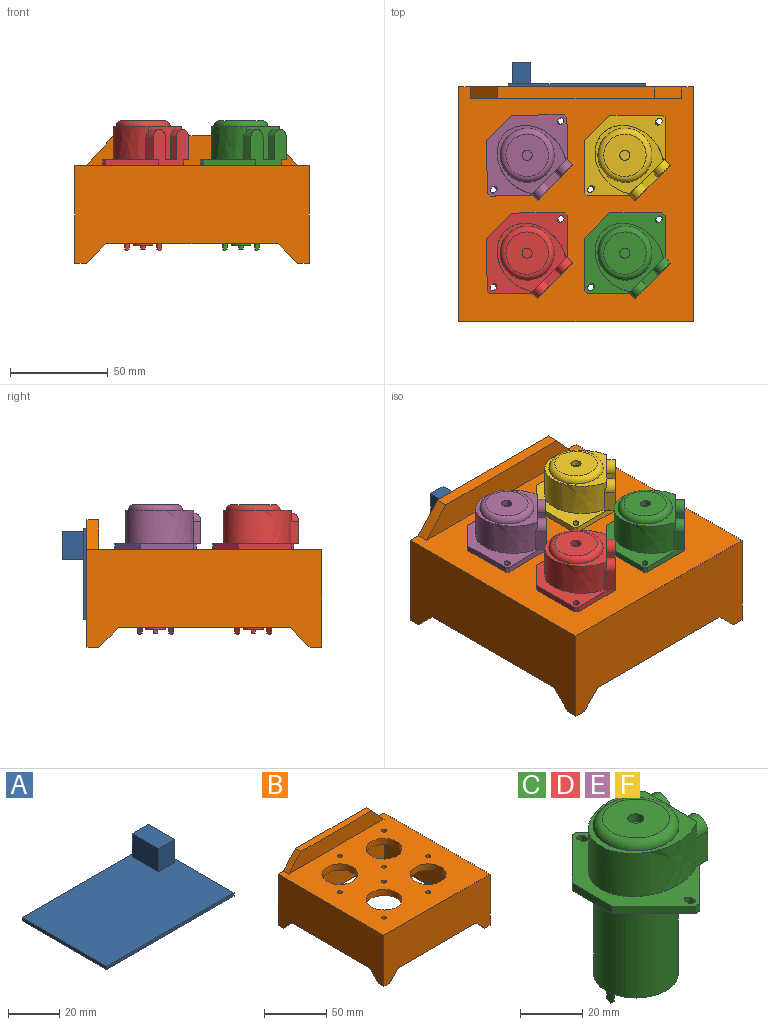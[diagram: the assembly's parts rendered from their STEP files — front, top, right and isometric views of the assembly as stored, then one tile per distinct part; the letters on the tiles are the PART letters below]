
ASSEMBLY  parts=6 mates=5
PART A: 11 faces, bbox 70x46.5x12.7 mm
  f0: plane 70x46.5mm, normal (0,0,1), area 3128.7mm2, adj f1,f2,f3,f4,f6,f7,f8,f9
  f1: plane 46.5x1.56mm, normal (-1,0,0), area 72.5mm2, adj f0,f2,f4,f5
  f2: plane 70x1.56mm, normal (0,-1,0), area 109.2mm2, adj f0,f1,f3,f5
  f3: plane 46.5x1.56mm, normal (1,0,0), area 72.5mm2, adj f0,f2,f4,f5
  f4: plane 70x1.56mm, normal (0,1,0), area 109.2mm2, adj f0,f1,f3,f5
  f5: plane 70x46.5mm, normal (0,0,-1), area 3255mm2, adj f1,f2,f3,f4
  f6: plane 11.09x8.83mm, normal (0,1,0), area 97.9mm2, adj f0,f7,f9,f10
  f7: plane 14.3x11.09mm, normal (-1,0,0), area 158.6mm2, adj f0,f6,f8,f10
  f8: plane 11.09x8.83mm, normal (0,-1,0), area 97.9mm2, adj f0,f7,f9,f10
  f9: plane 14.3x11.09mm, normal (1,0,0), area 158.6mm2, adj f0,f6,f8,f10
  f10: plane 14.3x8.83mm, normal (0,0,1), area 126.3mm2, adj f6,f7,f8,f9
PART B: 42 faces, bbox 120x120x65.3 mm
  f0: plane 88x6mm, normal (0,0,-1), area 528mm2, adj f9,f17,f19,f23
  f1: plane 88x6mm, normal (0,0,-1), area 528mm2, adj f3,f4,f8,f21
  f2: plane 88x6mm, normal (0,0,-1), area 528mm2, adj f5,f6,f7,f22
  f3: plane 10x10mm, normal (0,-0.71,-0.71), area 84.9mm2, adj f1,f8,f15,f21
  f4: plane 10x10mm, normal (0,0.71,-0.71), area 84.9mm2, adj f1,f8,f16,f21
  f5: plane 10x10mm, normal (-0.71,0,-0.71), area 84.9mm2, adj f2,f7,f16,f22
  f6: plane 10x10mm, normal (0.71,0,-0.71), area 84.9mm2, adj f2,f7,f13,f22
  f7: plane 120x50mm, normal (0,-1,0), area 5020mm2, adj f2,f5,f6,f8,f10,f12,f13,f16
  f8: plane 120x50mm, normal (1,0,0), area 5020mm2, adj f1,f3,f4,f7,f9,f12,f15,f16
  f9: plane 120x65.25mm, normal (0,1,0), area 6455mm2, adj f0,f8,f10,f12,f14,f15,f17,f19
  f10: plane 120x50mm, normal (-1,0,0), area 5020mm2, adj f7,f9,f11,f12,f13,f14,f18,f20
  f11: plane 88x6mm, normal (0,0,-1), area 528mm2, adj f10,f18,f20,f24
  f12: plane 120x120mm, normal (0,0,1), area 11088.6mm2, adj f7,f8,f9,f10,f26,f27,f28,f29
  f13: plane 6x6mm, normal (0,0,-1), area 36mm2, adj f6,f7,f10,f18
  f14: plane 6x6mm, normal (0,0,-1), area 36mm2, adj f9,f10,f19,f20
  f15: plane 6x6mm, normal (0,0,-1), area 36mm2, adj f3,f8,f9,f17
  f16: plane 6x6mm, normal (0,0,-1), area 36mm2, adj f4,f5,f7,f8
  f17: plane 10x10mm, normal (-0.71,0,-0.71), area 84.9mm2, adj f0,f9,f15,f23
  f18: plane 10x10mm, normal (0,0.71,-0.71), area 84.9mm2, adj f10,f11,f13,f24
  f19: plane 10x10mm, normal (0.71,0,-0.71), area 84.9mm2, adj f0,f9,f14,f23
  f20: plane 10x10mm, normal (0,-0.71,-0.71), area 84.9mm2, adj f10,f11,f14,f24
  f21: plane 108x44mm, normal (-1,0,0), area 3772mm2, adj f1,f3,f4,f22,f23,f25
  f22: plane 108x44mm, normal (0,1,0), area 3772mm2, adj f2,f5,f6,f21,f24,f25
  f23: plane 108x44mm, normal (0,-1,0), area 3772mm2, adj f0,f17,f19,f21,f24,f25
  f24: plane 108x44mm, normal (1,0,0), area 3772mm2, adj f11,f18,f20,f22,f23,f25
  f25: plane 108x108mm, normal (0,0,-1), area 9000.6mm2, adj f21,f22,f23,f24,f26,f27,f28,f29
  f26: cylinder r=14.3mm len=28.6mm, axis (0,0,1), area 539.1mm2, adj f12,f25
  f27: cylinder r=1.93mm len=6mm, axis (0,0,1), area 72.8mm2, adj f12,f25
  f28: cylinder r=1.93mm len=6mm, axis (0,0,1), area 72.8mm2, adj f12,f25
  f29: cylinder r=1.93mm len=6mm, axis (0,0,1), area 72.8mm2, adj f12,f25
  f30: cylinder r=14.3mm len=28.6mm, axis (0,0,1), area 539.1mm2, adj f12,f25
  f31: cylinder r=14.3mm len=28.6mm, axis (0,0,1), area 539.1mm2, adj f12,f25
  f32: cylinder r=14.3mm len=28.6mm, axis (0,0,1), area 539.1mm2, adj f12,f25
  f33: cylinder r=1.93mm len=6mm, axis (0,0,1), area 72.8mm2, adj f12,f25
  f34: cylinder r=1.93mm len=6mm, axis (0,0,1), area 72.8mm2, adj f12,f25
  f35: cylinder r=1.93mm len=6mm, axis (0,0,1), area 72.8mm2, adj f12,f25
  f36: cylinder r=1.93mm len=6mm, axis (0,0,1), area 72.8mm2, adj f12,f25
  f37: cylinder r=1.93mm len=6mm, axis (0,0,1), area 72.8mm2, adj f12,f25
  f38: plane 80.2x6mm, normal (0,0,1), area 481.2mm2, adj f9,f39,f40,f41
  f39: plane 15.25x13.9mm, normal (0.74,0,0.67), area 123.8mm2, adj f9,f12,f38,f41
  f40: plane 15.25x13.9mm, normal (-0.74,0,0.67), area 123.8mm2, adj f9,f12,f38,f41
  f41: plane 108x15.25mm, normal (0,-1,0), area 1435mm2, adj f12,f38,f39,f40
PART C: 54 faces, bbox 40x56.2x66.7 mm
  f0: plane 8x4.3mm, normal (0,0,1), area 34.4mm2, adj f28,f40,f48,f53
  f1: extruded ~31.62x31.61mm, area 1347.8mm2, adj f2,f40,f41,f46,f49,f51,f52
  f2: plane 56.22x36.3mm, normal (0,0,1), area 571.1mm2, adj f1,f23,f24,f25,f26,f27,f29,f30
  f3: cylinder r=13.67mm len=38.15mm, axis (0,0,1), area 3275.5mm2, adj f4,f39
  f4: plane 27.33x27.33mm, normal (0,0,-1), area 505.1mm2, adj f3,f5,f9,f10,f11,f12,f14,f15
  f5: cylinder r=5mm len=10mm, axis (0,0,1), area 81.7mm2, adj f4,f6
  f6: plane 10x10mm, normal (0,0,-1), area 74.6mm2, adj f5,f7
  f7: cylinder r=1.12mm len=2.25mm, axis (0,0,1), area 14.1mm2, adj f6,f8
  f8: plane 2.25x2.25mm, normal (0,0,-1), area 4mm2, adj f7
  f9: plane 4.5x0.53mm, normal (0,-1,0), area 2.4mm2, adj f4,f10,f12,f22
  f10: plane 5.5x2.85mm, normal (-1,0,0), area 14.7mm2, adj f4,f9,f11,f13,f21,f22
  f11: plane 4.5x0.53mm, normal (0,1,0), area 2.4mm2, adj f4,f10,f12,f21
  f12: plane 5.5x2.85mm, normal (1,0,0), area 14.7mm2, adj f4,f9,f11,f13,f21,f22
  f13: plane 0.85x0.53mm, normal (0,0,-1), area 0.5mm2, adj f10,f12,f21,f22
  f14: plane 4.5x0.53mm, normal (0,-1,0), area 2.4mm2, adj f4,f15,f17,f20
  f15: plane 5.5x2.85mm, normal (-1,0,0), area 14.7mm2, adj f4,f14,f16,f18,f19,f20
  f16: plane 4.5x0.53mm, normal (0,1,0), area 2.4mm2, adj f4,f15,f17,f19
  f17: plane 5.5x2.85mm, normal (1,0,0), area 14.7mm2, adj f4,f14,f16,f18,f19,f20
  f18: plane 0.85x0.53mm, normal (0,0,-1), area 0.5mm2, adj f15,f17,f19,f20
  f19: plane 1x1mm, normal (0,0.71,-0.71), area 0.7mm2, adj f15,f16,f17,f18
  f20: plane 1x1mm, normal (0,-0.71,-0.71), area 0.7mm2, adj f14,f15,f17,f18
  f21: plane 1x1mm, normal (0,0.71,-0.71), area 0.7mm2, adj f10,f11,f12,f13
  f22: plane 1x1mm, normal (0,-0.71,-0.71), area 0.7mm2, adj f9,f10,f12,f13
  f23: plane 19.01x19.01mm, normal (-0.71,0.71,0), area 80.7mm2, adj f2,f24,f38,f39
  f24: plane 18.2x3mm, normal (-1,0,0), area 54.6mm2, adj f2,f23,f25,f39
  f25: plane 19.01x19.01mm, normal (-0.71,-0.71,0), area 80.7mm2, adj f2,f24,f26,f39
  f26: plane 3x1.98mm, normal (0,-1,0), area 5.9mm2, adj f2,f25,f27,f39
  f27: plane 19.01x19.01mm, normal (0.71,-0.71,0), area 80.7mm2, adj f2,f26,f28,f39,f47
  f28: plane 25.6x18.65mm, normal (1,0,0), area 313.4mm2, adj f0,f27,f29,f39,f46,f47,f48,f49
  f29: plane 19.01x19.01mm, normal (0.71,0.71,0), area 80.7mm2, adj f2,f28,f38,f39,f50
  f30: plane 3x1.09mm, normal (1,0,0), area 3.3mm2, adj f2,f31,f36,f39
  f31: cylinder r=1.38mm len=3mm, axis (0,0,-1), area 13mm2, adj f2,f30,f32,f39
  f32: plane 3x1.09mm, normal (-1,0,0), area 3.3mm2, adj f2,f31,f36,f39
  f33: plane 3x1.09mm, normal (-1,0,0), area 3.3mm2, adj f2,f34,f37,f39
  f34: cylinder r=1.38mm len=3mm, axis (0,0,-1), area 13mm2, adj f2,f33,f35,f39
  f35: plane 3x1.09mm, normal (1,0,0), area 3.3mm2, adj f2,f34,f37,f39
  f36: cylinder r=1.38mm len=3mm, axis (0,0,-1), area 13mm2, adj f2,f30,f32,f39
  f37: cylinder r=1.38mm len=3mm, axis (0,0,-1), area 13mm2, adj f2,f33,f35,f39
  f38: plane 3x1.98mm, normal (0,1,0), area 5.9mm2, adj f2,f23,f29,f39
  f39: plane 56.22x40mm, normal (0,0,-1), area 921.4mm2, adj f3,f23,f24,f25,f26,f27,f28,f29
  f40: plane 24x17mm, normal (1,0,0), area 169.9mm2, adj f0,f1,f41,f48,f49,f52,f53
  f41: plane 31.62x31.61mm, normal (0,0,1), area 238.8mm2, adj f1,f40,f45
  f42: cylinder r=2.59mm len=5.18mm, axis (0,0,-1), area 48.8mm2, adj f43,f44
  f43: plane 21.66x21.66mm, normal (0,0,1), area 347.4mm2, adj f42,f45
  f44: plane 5.18x5.18mm, normal (0,0,1), area 21.1mm2, adj f42
  f45: torus R=10.83mm, axis (0,0,1), area 377.2mm2, adj f41,f43
  f46: plane 11.25x5.53mm, normal (0,-1,0), area 62.2mm2, adj f1,f2,f28,f47,f49
  f47: plane 3.7x3.7mm, normal (0,0,-1), area 6.8mm2, adj f27,f28,f46
  f48: plane 11.25x4.3mm, normal (0,1,0), area 48.4mm2, adj f0,f28,f40,f49
  f49: cylinder r=4.4mm len=8.8mm, axis (-1,0,0), area 61.6mm2, adj f1,f28,f40,f46,f48
  f50: plane 3.7x3.7mm, normal (0,0,-1), area 6.8mm2, adj f28,f29,f51
  f51: plane 11.25x5.53mm, normal (0,1,0), area 62.2mm2, adj f1,f2,f28,f50,f52
  f52: cylinder r=4.4mm len=8.8mm, axis (-1,0,0), area 61.6mm2, adj f1,f28,f40,f51,f53
  f53: plane 11.25x4.3mm, normal (0,-1,0), area 48.4mm2, adj f0,f28,f40,f52
PART D: same geometry as C
PART E: same geometry as C
PART F: same geometry as C
PLACE A rot(axis=(0,-0.71,-0.71),180deg) t=(36.16,60.93,36.4)mm
PLACE B t=(60.55,-59.07,72.36)mm fixed
PLACE C rot(axis=(0,0,-1),45deg) t=(25.55,-24.07,72.36)mm
PLACE D rot(axis=(0,0,-1),44.6deg) t=(-24.45,-24.07,72.36)mm
PLACE E rot(axis=(0,0,-1),44.4deg) t=(-24.45,25.93,72.36)mm
PLACE F rot(axis=(0,0,-1),45.1deg) t=(25.55,25.93,72.36)mm
MATE planar A.f5 <-> B.f9  axis (0,-1,0) through (1.16,60.93,59.65)mm
MATE revolute F.f3 <-> B.f31  axis (0,0,1) through (25.55,25.93,72.36)mm
MATE revolute D.f3 <-> B.f26  axis (0,0,1) through (-24.45,-24.07,72.36)mm
MATE revolute E.f3 <-> B.f32  axis (0,0,1) through (-24.45,25.93,72.36)mm
MATE revolute C.f3 <-> B.f30  axis (0,0,1) through (25.55,-24.07,72.36)mm
